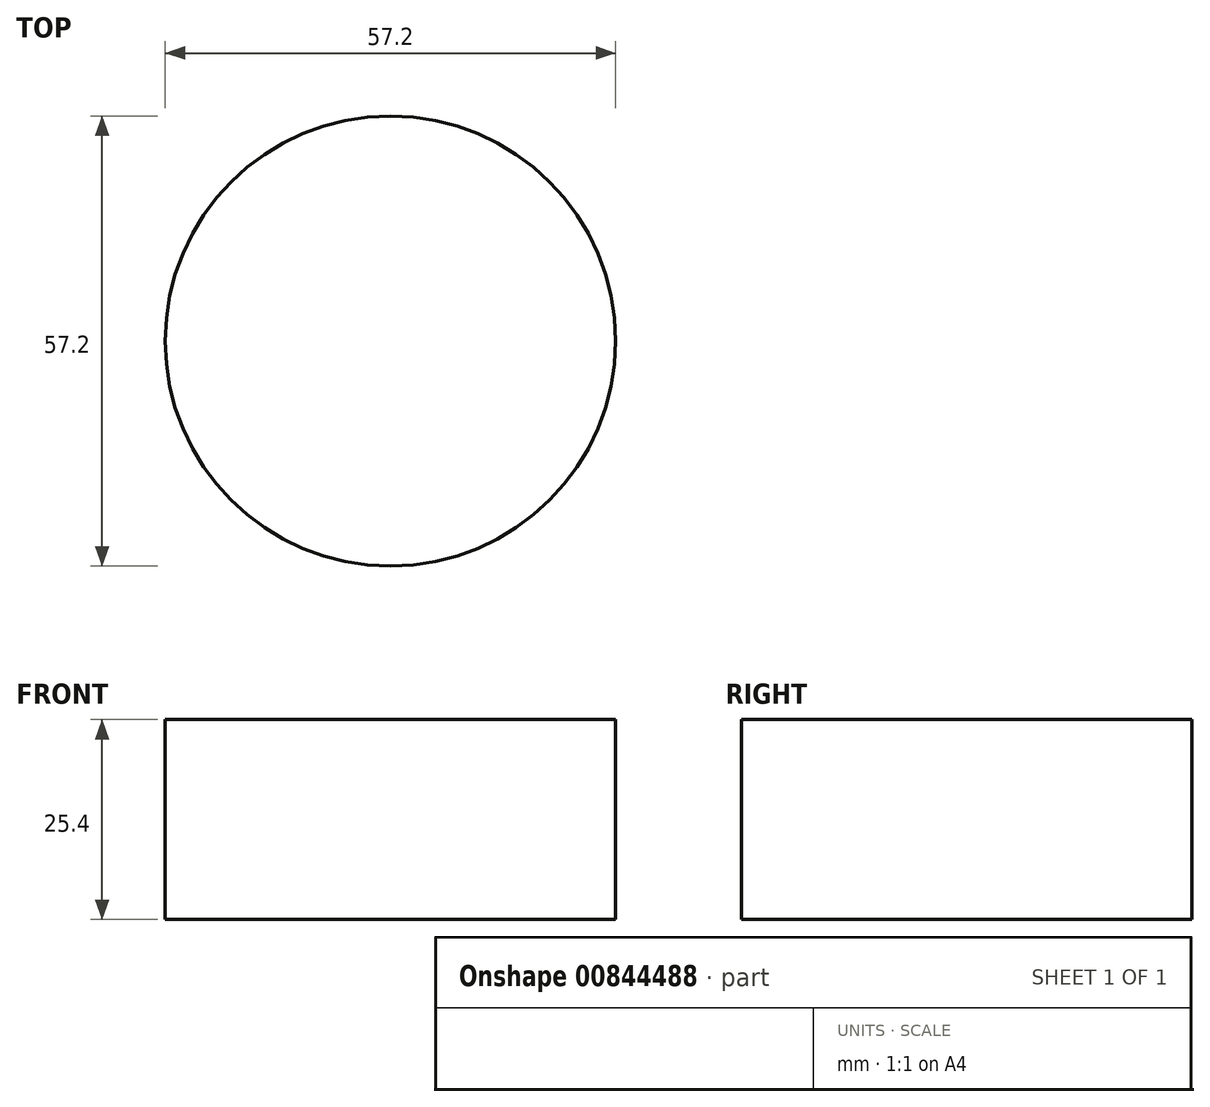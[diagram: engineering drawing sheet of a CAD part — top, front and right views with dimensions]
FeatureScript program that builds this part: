
annotation { "Feature Type Name" : "Feature", "Feature Type Description" : "" }
export const myFeature = defineFeature(function(context is Context, id is Id, definition is map)
    precondition{}
    {
        {
            var Q0;
            Q0=qCreatedBy(makeId("Top.planeOp"),FACE);
            var sketch = newSketch(context, id + "F0", { "sketchPlane" : qUnion([Q0])});
            skCircle(sketch, "E0", {"center": v(0, 0) * mm, "radius": 28.6 * mm});
            skSolve(sketch);
        }
        {
            var Q0;
            Q0=makeQuery(id+"F0.imprint","IMPRINT",FACE,{"disambiguationData":[TD([[makeQuery(id+"F0.imprint","IMPRINT",EDGE,{"derivedFrom":sQuery(id+"F0.wireOp",EDGE,"E0")}),1.0]])]});
            extrude(context, id + "F1", {"entities" : qUnion([Q0]), "depth" : 25.4 * mm, "offsetDistance" : 25.4 * mm});
        }
    });
